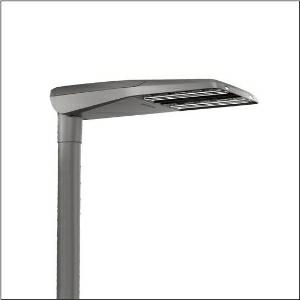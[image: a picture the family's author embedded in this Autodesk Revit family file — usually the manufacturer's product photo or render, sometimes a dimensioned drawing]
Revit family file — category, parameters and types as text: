
# Revit family: streetlight_sl_11_iq_midi___st1_0p1_0_5xc3k51f08me_0ac4
name_source: partatom
category: Lighting Fixtures
units: mm (PartAtom-declared; Revit-internal decimal feet)

## family parameters
Cut with Voids When Loaded = No
Host = Face
Light Source = No
Part Type = Normal
Room Calculation Point = No
Round Connector Dimension = Use Diameter
Shared = No

## types (1)
- --- (1 x LED, 17550 lm, 124.7 W, 3000K)
    Apparent Load = 125 VA
    CIE Flux Codes = 32 65 95 100 100
    Color Rendering = 70
    Color Temperature = 3000K
    Default Elevation = 1800 mm
    Description = Streetlight SL 11 iQ midi, mast luminaire, primary light control with 3 zone facetted reflector, of plastic, silver coated, highly specular, primary optical cover: cover, of PMMA, transparent, light distribution: ST1.0P1.0, light emission: direct distribution, primary light characteristic: asymmetric, installation type: post-top, side-entry, lamps: LED, High Power LED, rated values: 17.550lm | 124,7W | 140,7lm/W (begin service life); end service life: 17.550lm | 132,2W; at 50% lumin. flux: 8.775lm | 57,2W | 153,4lm/W, colour temperature: 3000K, colour rendering: CRI > 70, light colour: 730, light setting 1 begin service life: 100% | 17.550lm | 124,7W | 140,7lm/W | 3.000K, light setting 1 end service life: 132,2W, further light settings possible, control: Street-Remote, Auto-Match, Temp-Guard, Lumen-Switch, Night-Set, Smart-Wire, Light-Fading, Desk-Remote (wireless, voltage-free reading and setting of iQ features in the workshop via application-optimized NFC function/RFID function), optimised constant luminous flux control (CLO 2.0), with cable H07RN-F 3x 1.5mm², mains connection: 230..240V, AC, 50/60Hz, connection cable pre-assembled, cable length: 12,5m, luminaire housing, of diecast aluminium, powder-coated, SITECO metallic grey (DB 702S), please order mast flange separately, inclination adjustable without tools: 0°, 5°, 10°, 15° (post-top) | 0°, -5°, -10°, -15° (side-entry), sealing non-destructively replaceable, multi-level sealing system, length: 780mm, width: 376mm, height: 118mm, mast flange for spigot size: 42mm (side-entry): 5XC10008XM4, 60/48mm (side-entry/post-top): 5XC10108XM2, 76/60mm (side-entry/post-top): 5XC10108XM1, equipment: Power, protection rating (complete): IP66, insulation class (complete): insulation class II (safety insulation), certification: CE, ENEC, ENEC+, VDE, impact resistance: IK10, permissible operating ambient temperature for outdoor applications: -25..+50°C, standard-compliant lighting for roads and squares, Environmental Product Declaration (EPD) tested and certified by an independent institute, packaging unit: 1 piece

Light Distribution: ST1.0P1.0
    Height = 118 mm
    Lamp = 1 x LED
    Lamp Light Flux = 17550 lm
    Lamp Power = 124.7 W
    Lamp count = 1
    Length = 780 mm
    Luminous efficacy = 141 lm/W
    Manufacturer = Siteco
    ModVariant = No
    Model = 5XC3K51F08ME
    Number of Poles = 1
    OnlyDefault = Yes
    Power Factor = 1
    Product Name = Streetlight SL 11 iQ midi | ST1.0P1.0
    Product group = mast luminaire | pylon top
    ProductGroupID = 6100
    Protection Class = Protection class II
    Protection Degree = IP 66
    RLX_Detail_Level = 1
    RLX_Emergency_Light_Flux = 0 lm
    RLX_Emergency_Type = 0
    RLX_Emergency_Type_DB = No
    RlxData = <blob elided: 70885 chars, md5=240e211f>
    Socket = socket
    Standby Power = 0 W
    System Light Flux = 17550 lm
    System Power = 125 W
    Type Comments = factory setting: luminous flux: 100 % | dim-lin: 254 | 557 mA
    Type Image = l_1005960.jpg
    URL = http://relux.com
    VarID = @adj_048075
    Voltage = 0 V
    Weight = 0.00 kg
    Width = 376 mm

## geometry (parser evidence)
native form markers: Blend x4, Sweep x9
no freeform markers — native parametric forms only
